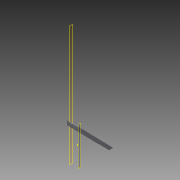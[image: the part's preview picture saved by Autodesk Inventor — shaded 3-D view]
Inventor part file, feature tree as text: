
AUTODESK INVENTOR PART (.ipt)
format: ipt  version: 2015 (Build 190159000, 159)  size: 150,528 bytes
history: native  units: in
note: dims shown in document units (in); Inventor stores cm internally (conversion verified against a paired STEP export)
features: sketch x4, extrude x3, plane x2, pattern_linear x1, reference x1, projected_geometry x1
ambient origin geometry x8: Origin, YZ Plane, XZ Plane, XY Plane, X Axis, Y Axis, Z Axis, Center Point
bodies: Solid1 (feature_tree)
feature tree (12):
  plane  "Work Plane1"
  extrude  "Extrusion1"  Depth=1.5in TaperAngle=0.0deg
  plane  "Work Plane2"
  extrude  "Extrusion2"  Depth=1.5in
  sketch  "Sketch4"  dims[d6=19.5in d7=9.0in]
  extrude  "Extrusion3"  Depth=9.0in
  pattern_linear  "Rectangular Pattern1"  Spacing1=1.5in  [1 undecoded]
  sketch  "Sketch1"  dims[d0=9.25in d1=1.5in d2=0.0in]
  reference  "Reference1"
  sketch  "Sketch2"  dims[d3=1.5in d4=0.0in d5=3.5in]
  projected_geometry  "Projected Loop1"
  sketch  "Sketch5"  dims[d8=1.5in d9=1.5in d10=0.0in d11=6.2992in d13=9.25in]
note: 1 required parameter value undecoded (feature->parameter linkage not recoverable at this tier; creation-order binding heuristic only, values carry confidence <= 0.55)
